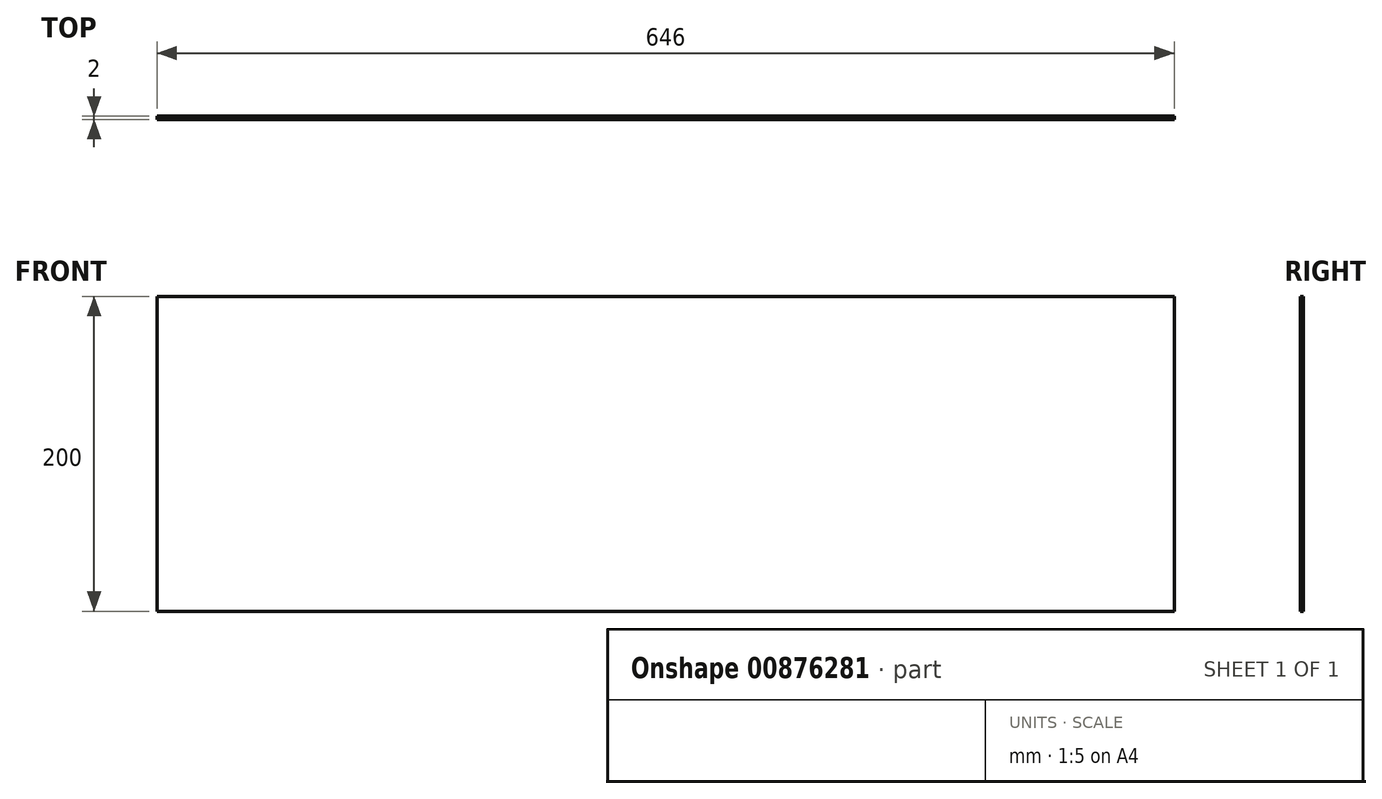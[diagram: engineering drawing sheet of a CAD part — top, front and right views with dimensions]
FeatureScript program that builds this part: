
annotation { "Feature Type Name" : "Feature", "Feature Type Description" : "" }
export const myFeature = defineFeature(function(context is Context, id is Id, definition is map)
    precondition{}
    {
        {
            var Q0;
            Q0=qCreatedBy(makeId("Front.planeOp"),FACE);
            var sketch = newSketch(context, id + "F0", { "sketchPlane" : qUnion([Q0])});
            skLineSegment(sketch, "E0.bottom", {"start": v(-323, 100) * mm, "end": v(323, 100) * mm});
            skLineSegment(sketch, "E0.top", {"start": v(-323, -100) * mm, "end": v(323, -100) * mm});
            skLineSegment(sketch, "E0.left", {"start": v(-323, 100) * mm, "end": v(-323, -100) * mm});
            skLineSegment(sketch, "E0.right", {"start": v(323, 100) * mm, "end": v(323, -100) * mm});
            skPoint(sketch, "E0.middle", {"position": v(0, 0) * mm});
            skSolve(sketch);
        }
        {
            var Q0;
            Q0=makeQuery(id+"F0.imprint","IMPRINT",FACE,{"disambiguationData":[TD([[makeQuery(id+"F0.imprint","IMPRINT",EDGE,{"derivedFrom":sQuery(id+"F0.wireOp",EDGE,"E0.bottom")}),-1.0]])]});
            extrude(context, id + "F1", {"entities" : qUnion([Q0]), "depth" : 2 * mm, "offsetDistance" : 25.4 * mm});
        }
    });
